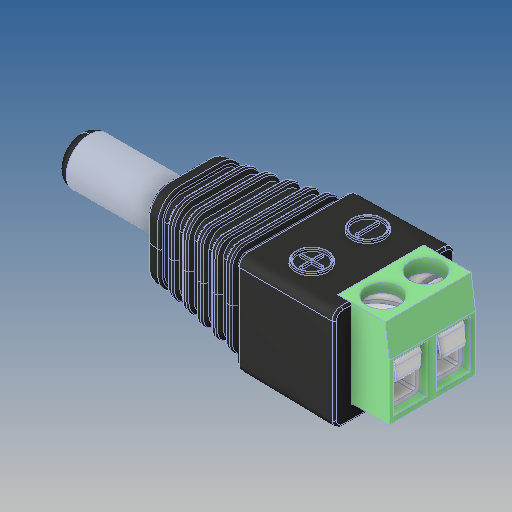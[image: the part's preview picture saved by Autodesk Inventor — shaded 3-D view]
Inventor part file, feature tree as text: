
AUTODESK INVENTOR PART (.ipt)
format: ipt  version: 2018 (Build 220112000, 112)  size: 1,449,984 bytes
history: native  units: mm
features: fillet x1
ambient origin geometry x8: Origin, YZ Plane, XZ Plane, XY Plane, X Axis, Y Axis, Z Axis, Center Point
bodies: Solid1 (feature_tree)
feature tree (1):
  fillet  "Fillet5"  [1 undecoded]
note: 1 required parameter value undecoded (feature->parameter linkage not recoverable at this tier; creation-order binding heuristic only, values carry confidence <= 0.55)
